AUTODESK INVENTOR PART (.ipt)
format: ipt  version: 2019 (Build 230136000, 136)  size: 108,032 bytes
history: native  units: in
note: dims shown in document units (in); Inventor stores cm internally (conversion verified against a paired STEP export)
features: other x19, sketch x2, plane x1
ambient origin geometry x4: Origin, YZ Plane, XZ Plane, XY Plane
feature tree (22):
  parser-record x1  (decoder bookkeeping rows leaked as tree rows — omitted from the tree; the rows remain in map.json)
  other  "d offset"
  other  "theta offset"
  other  "r_offset"
  other  "alpha offset"
  sketch  "Sketch4"  dims[d0=0.0in d1=0.0in d2=0.0in d3=0.0in d4=0.0in d5=0.0in d7=7.2441in d8=0.0in d11=0.0in d12=90.0deg d13=0.0394in d14=0.0394in d15=0.0in d16=0.0in d17=0.0in d18=0.0in d19=0.0in d20=0.0in]
  sketch  "3D Sketch2"
  plane  "Work Plane5"
  other  "UCS3: YZ Plane"
  other  "UCS3: XZ Plane"
  other  "UCS3: XY Plane"
  other  "UCS3: X Axis"
  other  "UCS3: Y Axis"
  other  "UCS3: Z Axis"
  other  "UCS3: Center Point"
  other  "UCS4: YZ Plane"
  other  "UCS4: XZ Plane"
  other  "UCS4: XY Plane"
  other  "UCS4: X Axis"
  other  "UCS4: Y Axis"
  other  "UCS4: Z Axis"
  other  "UCS4: Center Point"
note: 1 file-system path scrubbed to <path> (originals preserved in map.json)
